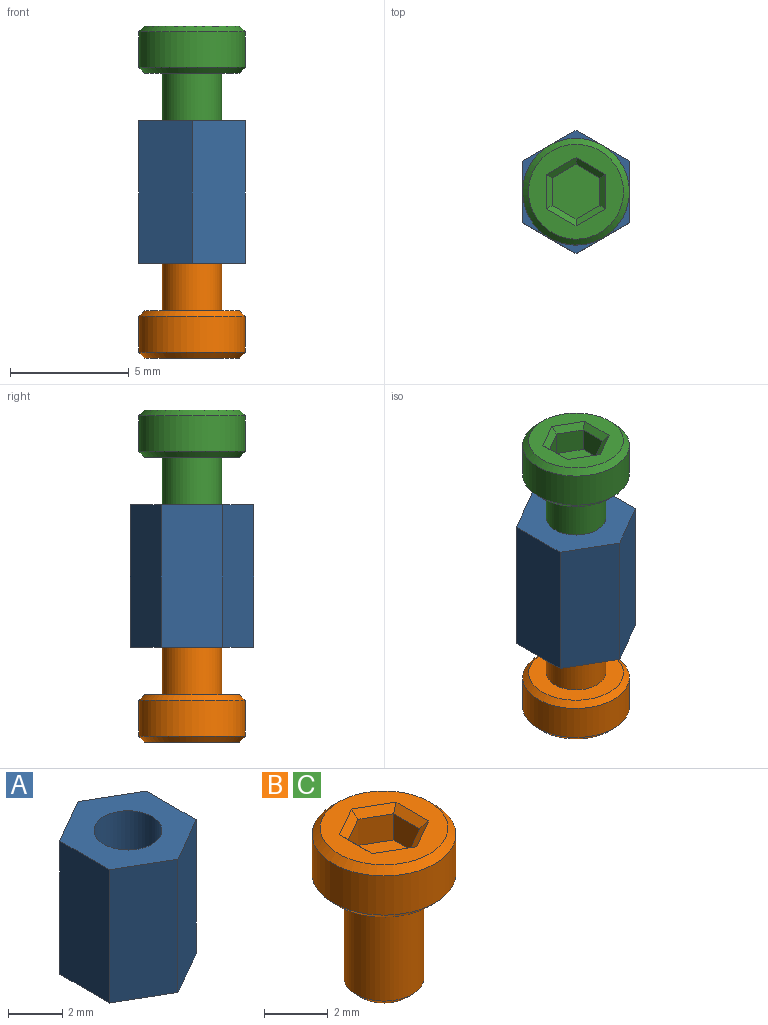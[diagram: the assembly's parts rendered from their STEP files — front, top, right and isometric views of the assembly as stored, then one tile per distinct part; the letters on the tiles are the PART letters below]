
ASSEMBLY  parts=3 mates=2
PART A: 9 faces, bbox 4.5x5.2x6 mm
  f0: plane 6x2.6mm, normal (1,0,0), area 15.6mm2, adj f1,f6,f7,f8
  f1: plane 6x2.25mm, normal (0.5,0.87,0), area 15.6mm2, adj f0,f2,f7,f8
  f2: plane 6x2.25mm, normal (-0.5,0.87,0), area 15.6mm2, adj f1,f3,f7,f8
  f3: plane 6x2.6mm, normal (-1,0,0), area 15.6mm2, adj f2,f4,f7,f8
  f4: plane 6x2.25mm, normal (-0.5,-0.87,0), area 15.6mm2, adj f3,f6,f7,f8
  f5: cylinder r=1.25mm len=6mm, axis (0,0,1), area 47.1mm2, adj f7,f8
  f6: plane 6x2.25mm, normal (0.5,-0.87,0), area 15.6mm2, adj f0,f4,f7,f8
  f7: plane 5.2x4.5mm, normal (0,0,-1), area 12.6mm2, adj f0,f1,f2,f3,f4,f5,f6
  f8: plane 5.2x4.5mm, normal (0,0,1), area 12.6mm2, adj f0,f1,f2,f3,f4,f5,f6
PART B: 21 faces, bbox 4.5x4.5x6 mm
  f0: plane 4x4mm, normal (0,0,1), area 7.2mm2, adj f12,f13,f14,f15,f16,f17,f18
  f1: cylinder r=1.25mm len=3.75mm, axis (0,0,1), area 29.5mm2, adj f4,f20
  f2: plane 2x2mm, normal (0,0,-1), area 3.1mm2, adj f20
  f3: cylinder r=2.25mm len=4.5mm, axis (0,0,-1), area 21.2mm2, adj f18,f19
  f4: plane 4x4mm, normal (0,0,-1), area 7.7mm2, adj f1,f19
  f5: plane 1x1mm, normal (-0.5,0.87,0), area 1.2mm2, adj f6,f10,f11,f17
  f6: plane 1.15x1mm, normal (-1,0,0), area 1.2mm2, adj f5,f7,f11,f15
  f7: plane 1x1mm, normal (-0.5,-0.87,0), area 1.2mm2, adj f6,f8,f11,f13
  f8: plane 1x1mm, normal (0.5,-0.87,0), area 1.2mm2, adj f7,f9,f11,f12
  f9: plane 1.15x1mm, normal (1,0,0), area 1.2mm2, adj f8,f10,f11,f14
  f10: plane 1x1mm, normal (0.5,0.87,0), area 1.2mm2, adj f5,f9,f11,f16
  f11: plane 2.31x2mm, normal (0,0,1), area 3.5mm2, adj f5,f6,f7,f8,f9,f10
  f12: plane 1.25x0.87mm, normal (0.35,-0.61,0.71), area 0.5mm2, adj f0,f8,f13,f14
  f13: plane 1.25x0.87mm, normal (-0.35,-0.61,0.71), area 0.5mm2, adj f0,f7,f12,f15
  f14: plane 1.44x0.25mm, normal (0.71,0,0.71), area 0.5mm2, adj f0,f9,f12,f16
  f15: plane 1.44x0.25mm, normal (-0.71,0,0.71), area 0.5mm2, adj f0,f6,f13,f17
  f16: plane 1.25x0.87mm, normal (0.35,0.61,0.71), area 0.5mm2, adj f0,f10,f14,f17
  f17: plane 1.25x0.87mm, normal (-0.35,0.61,0.71), area 0.5mm2, adj f0,f5,f15,f16
  f18: cone r=2mm half-angle=45deg, axis (0,0,-1), area 4.7mm2, adj f0,f3
  f19: cone r=2.25mm half-angle=45deg, axis (0,0,1), area 4.7mm2, adj f3,f4
  f20: cone r=1.25mm half-angle=45deg, axis (0,0,1), area 2.5mm2, adj f1,f2
PART C: same geometry as B
PLACE A at identity
PLACE B rot(axis=(0,1,0),180deg) t=(0,0,-8)mm
PLACE C t=(0,0,2)mm
MATE fastened B.f1 <-> A.f5  axis (0,0,1) through (0,0,-8)mm
MATE fastened C.f1 <-> A.f5  axis (0,0,-1) through (0,0,2)mm
